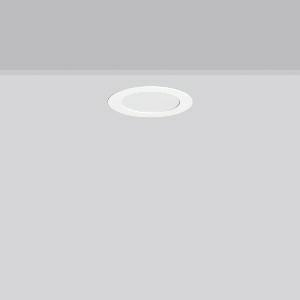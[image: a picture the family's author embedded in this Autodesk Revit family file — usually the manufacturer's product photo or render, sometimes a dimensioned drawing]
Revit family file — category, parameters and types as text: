
# Revit family: toledo_flat__round_e_901807_002_76_fab3
name_source: partatom
category: Lighting Fixtures
units: mm (PartAtom-declared; Revit-internal decimal feet)

## family parameters
Cut with Voids When Loaded = No
Host = Face
Light Source = No
Part Type = Normal
Room Calculation Point = No
Round Connector Dimension = Use Diameter
Shared = No

## types (1)
- MultiLumen 1 (1 x LED Modul 840, 570 lm, 4000)
    Apparent Load = 5 VA
    CIE Flux Codes = 48 79 96 100 100
    Color Rendering = 80
    Color Temperature = 4000
    Default Elevation = 1800 mm
    Description = Series: TOLEDO FLAT+ round
Flexible round recessed multifunction downlight. Housing: sheet steel, powder-coated. Luminaire frame: aluminium, powder-coated. Light guide and diffuser made of non-yellowing PMMA, opal matt. LED backlight technology for homogeneous illumination of the entire light-emitting surface. MultiColour: Colour temperature individually adjustable either 3000 K or 4000 K via switching element. Factory setting is 4000 K. MultiLumen: 4 steps adjustable luminous flux. Factory setting is step 2. Suitable for Recessed ceiling mounting. Ceiling installation with spring system. Can be directly covered with thermal insulation material (applies only to the lower lumen levels). Including separate LED converter with connecting cable 250 mm. Suitable for through wiring as standard. Surface mounted housing as accessory for all sizes. 
Colour: white
Diameter: 165 mm
Height: 2 mm
Cut-out diameter: 152 mm
Recess height: 60 mm
Luminaire: recess height: 35 mm
Lamp: LED
Socket: without socket
Colour temperature: 3000K, 4000K
Colour rendering index (CRI): 80
System power: 4.5 W
Rated luminous flux: 570 lm
Luminous efficiency: 127 lm/W
System power 2: 6 W
Rated luminous flux 2: 720 lm
Luminous efficiency 2: 120 lm/W
System power 3: 8 W
Rated luminous flux 3: 1000 lm
Luminous efficiency 3: 125 lm/W
System power 4: 9.5 W
Rated luminous flux 4: 1150 lm
Luminous efficiency 4: 121 lm/W
Control gear: Converter, dimmable, DALI
Protection class: II
Type of protection: IP 54
    Height = 0 mm  [stored 0 ft]
    Lamp = 1 x LED Modul 840
    Lamp Light Flux = 570 lm
    Lamp count = 1
    Length = 165 mm
    Lifetime = 50000 h
    Luminous efficacy = 127 lm/W
    Manufacturer = RZB
    ModVariant = No
    Model = 901807.002.76
    Mounting Place = Ceiling
    Mounting Type = Recessed
    Number of Poles = 1
    OnlyDefault = Yes
    Power Factor = 1
    Product Name = TOLEDO FLAT+ round E
    Product group = Recessed downlights
    ProductGroupID = 402
    Protection Class = Protection class II
    Protection Degree = Degree of protection
    RLX_Detail_Level = 1
    RLX_Emergency_Light_Flux = 0 lm
    RLX_Emergency_Type = 0
    RLX_Emergency_Type_DB = No
    RlxData = <blob elided: 27429 chars, md5=9a31f5dc>
    Socket = socket
    Standby Power = 0 W
    System Light Flux = 570 lm
    System Power = 5 W
    Type Comments = MultiLumen 1
    Type Image = 901807.002.jpg
    URL = http://relux.com
    VarID = multilumen_1
    Voltage = 0 V
    Weight = 0.00 kg
    Width = 0 mm  [stored 0 ft]

note: [stored X ft] marks values corroborated as IEEE doubles in the binary element streams (Revit-internal decimal feet)

## geometry (parser evidence)
native form markers: Blend x4, Sweep x13
no freeform markers — native parametric forms only
